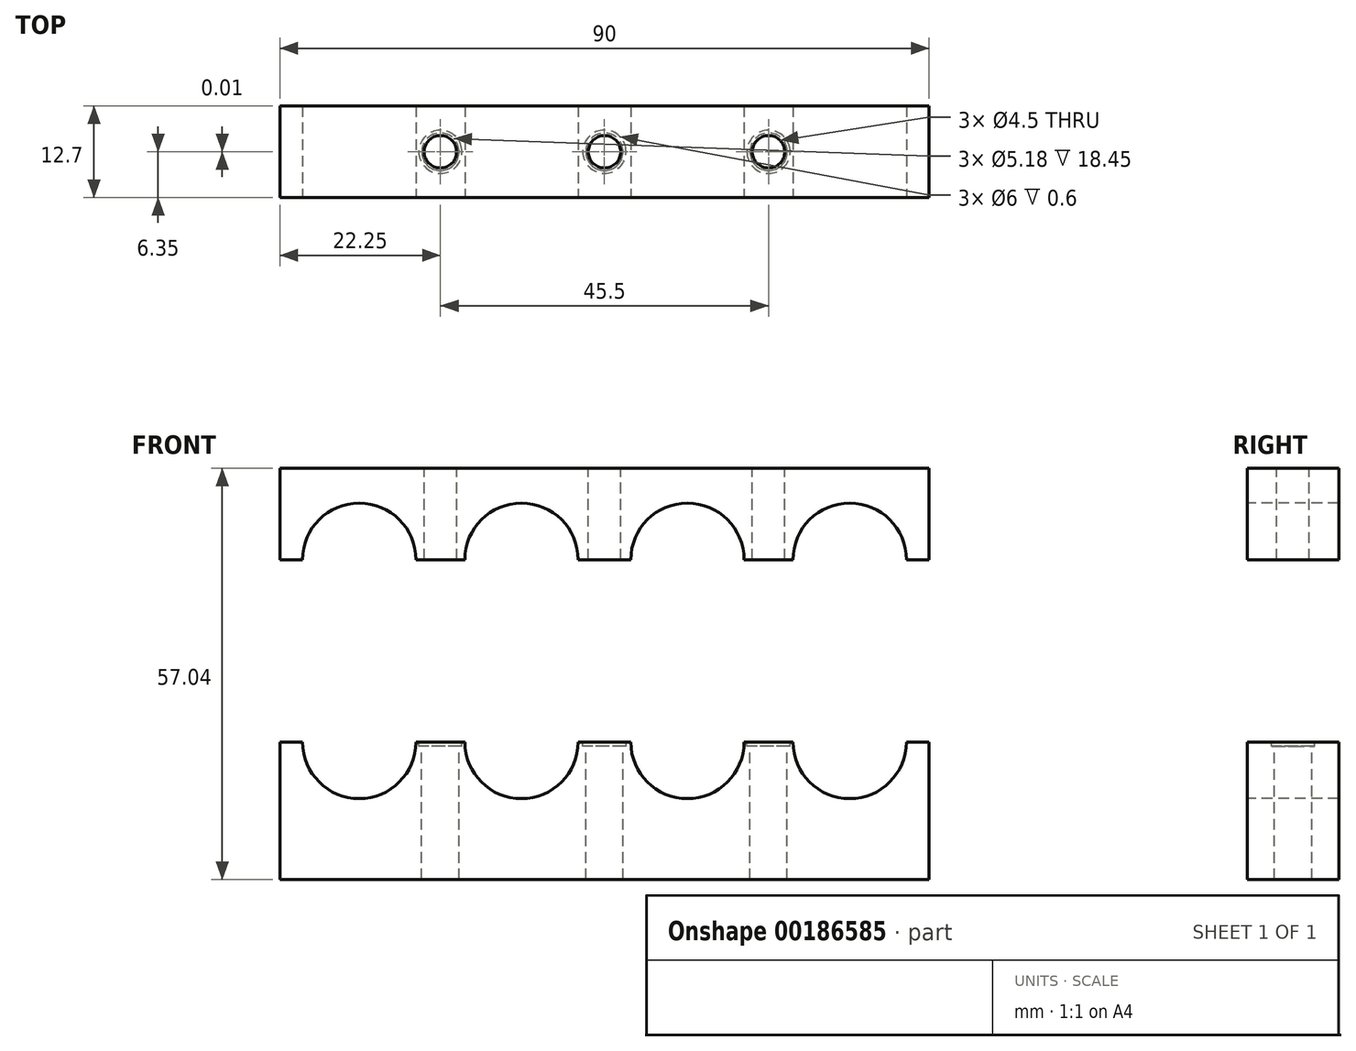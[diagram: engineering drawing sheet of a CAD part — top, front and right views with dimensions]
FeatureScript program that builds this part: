
annotation { "Feature Type Name" : "Feature", "Feature Type Description" : "" }
export const myFeature = defineFeature(function(context is Context, id is Id, definition is map)
    precondition{}
    {
        {
            var Q0;
            Q0=qCreatedBy(makeId("Front.planeOp"),FACE);
            var sketch = newSketch(context, id + "F0", { "sketchPlane" : qUnion([Q0])});
            skLineSegment(sketch, "E0.bottom", {"start": v(45, 9.52) * mm, "end": v(-45, 9.53) * mm});
            skLineSegment(sketch, "E0.top", {"start": v(45, -9.53) * mm, "end": v(-45, -9.52) * mm});
            skLineSegment(sketch, "E0.left", {"start": v(45, 9.52) * mm, "end": v(45, -9.53) * mm});
            skLineSegment(sketch, "E0.right", {"start": v(-45, 9.53) * mm, "end": v(-45, -9.52) * mm});
            skPoint(sketch, "E0.middle", {"position": v(0, 0) * mm});
            skSolve(sketch);
        }
        {
            var Q0;
            Q0 = qSketchRegion(id + "F0", true);
            extrude(context, id + "F1", {"entities" : qUnion([Q0]), "depth" : 12.7 * mm});
        }
        {
            var Q0;
            Q0=makeQuery(id+"F1.opExtrude","CAP_FACE",FACE,{"disambiguationData":[OSD([sQuery(id+"F0.wireOp",EDGE,"E0.bottom"),sQuery(id+"F0.wireOp",EDGE,"E0.top"),sQuery(id+"F0.wireOp",EDGE,"E0.left"),sQuery(id+"F0.wireOp",EDGE,"E0.right")])],"isStart":false});
            var sketch = newSketch(context, id + "F2", { "sketchPlane" : qUnion([Q0])});
            skCircle(sketch, "E1", {"center": v(-34, 9.52) * mm, "radius": 7.85 * mm});
            skCircle(sketch, "E2", {"center": v(-11.5, 9.52) * mm, "radius": 7.85 * mm});
            skCircle(sketch, "E3.MirrorC", {"center": v(11.5, 9.52) * mm, "radius": 7.85 * mm});
            skCircle(sketch, "E4.MirrorC", {"center": v(34, 9.52) * mm, "radius": 7.85 * mm});
            skSolve(sketch);
        }
        {
            var Q0;
            Q0 = qSketchRegion(id + "F2", true);
            extrude(context, id + "F3", {"entities" : qUnion([Q0]), "operationType" : NewBodyOperationType.REMOVE, "oppositeDirection" : true, "depth" : 25.4 * mm});
        }
        {
            var Q0;
            Q0=qCreatedBy(makeId("Front.planeOp"),FACE);
            var sketch = newSketch(context, id + "F4", { "sketchPlane" : qUnion([Q0])});
            skLineSegment(sketch, "E5.bottom", {"start": v(45, 34.81) * mm, "end": v(-45, 34.81) * mm});
            skLineSegment(sketch, "E5.top", {"start": v(45, 47.51) * mm, "end": v(-45, 47.51) * mm});
            skLineSegment(sketch, "E5.left", {"start": v(45, 34.81) * mm, "end": v(45, 47.51) * mm});
            skLineSegment(sketch, "E5.right", {"start": v(-45, 34.81) * mm, "end": v(-45, 47.51) * mm});
            skPoint(sketch, "E5.middle", {"position": v(0, 41.16) * mm});
            skSolve(sketch);
        }
        {
            var Q0;
            Q0=makeQuery(id+"F4.imprint","IMPRINT",FACE,{"disambiguationData":[TD([[makeQuery(id+"F4.imprint","IMPRINT",EDGE,{"derivedFrom":sQuery(id+"F4.wireOp",EDGE,"E5.bottom")}),-1.0]])]});
            extrude(context, id + "F5", {"entities" : qUnion([Q0]), "depth" : 12.7 * mm});
        }
        {
            var Q0;
            Q0=makeQuery(id+"F5.opExtrude","CAP_FACE",FACE,{"disambiguationData":[OSD([sQuery(id+"F4.wireOp",EDGE,"E5.bottom"),sQuery(id+"F4.wireOp",EDGE,"E5.top"),sQuery(id+"F4.wireOp",EDGE,"E5.left"),sQuery(id+"F4.wireOp",EDGE,"E5.right")])],"isStart":false});
            var sketch = newSketch(context, id + "F6", { "sketchPlane" : qUnion([Q0])});
            skCircle(sketch, "E6", {"center": v(-34, 34.81) * mm, "radius": 7.85 * mm});
            skCircle(sketch, "E7", {"center": v(-11.5, 34.81) * mm, "radius": 7.85 * mm});
            skCircle(sketch, "E8.MirrorC", {"center": v(11.5, 34.81) * mm, "radius": 7.85 * mm});
            skCircle(sketch, "E9.MirrorC", {"center": v(34, 34.81) * mm, "radius": 7.85 * mm});
            skSolve(sketch);
        }
        {
            var Q0;
            Q0 = qSketchRegion(id + "F6", true);
            extrude(context, id + "F7", {"entities" : qUnion([Q0]), "operationType" : NewBodyOperationType.REMOVE, "oppositeDirection" : true, "depth" : 25.4 * mm});
        }
        {
            var Q0;
            Q0=makeQuery(id+"F5.opExtrude","SWEPT_FACE",FACE,{"disambiguationData":[OSD([sQuery(id+"F4.wireOp",EDGE,"E5.top")])]});
            var sketch = newSketch(context, id + "F8", { "sketchPlane" : qUnion([Q0])});
            skCircle(sketch, "E10", {"center": v(-22.75, -6.35) * mm, "radius": 2.25 * mm});
            skCircle(sketch, "E11", {"center": v(0, -6.35) * mm, "radius": 2.25 * mm});
            skCircle(sketch, "E12", {"center": v(22.75, -6.35) * mm, "radius": 2.25 * mm});
            skSolve(sketch);
        }
        {
            var Q0;
            Q0 = qSketchRegion(id + "F8", true);
            extrude(context, id + "F9", {"entities" : qUnion([Q0]), "operationType" : NewBodyOperationType.REMOVE, "oppositeDirection" : true, "depth" : 25.4 * mm});
        }
        {
            var Q0;
            {var subQ0=sQuery(id+"F0.wireOp",EDGE,"E0.right");var subQ1=sQuery(id+"F0.wireOp",EDGE,"E0.left");var subQ2=sQuery(id+"F0.wireOp",EDGE,"E0.top");var subQ3=sQuery(id+"F0.wireOp",EDGE,"E0.bottom");Q0=makeQuery(id+"F3.boolean.opBoolean","SPLIT",FACE,{"disambiguationData":[TD([makeQuery(id+"F1.opExtrude","CAP_FACE",FACE,{"disambiguationData":[OSD([subQ3,subQ2,subQ1,subQ0])],"isStart":true}),makeQuery(id+"F1.opExtrude","CAP_FACE",FACE,{"disambiguationData":[OSD([subQ3,subQ2,subQ1,subQ0])],"isStart":false}),makeQuery(id+"F3.opExtrude","SWEPT_FACE",FACE,{"disambiguationData":[OSD([sQuery(id+"F2.wireOp",EDGE,"E1")])]}),makeQuery(id+"F3.opExtrude","SWEPT_FACE",FACE,{"disambiguationData":[OSD([sQuery(id+"F2.wireOp",EDGE,"E2")])]})])],"derivedFrom":makeQuery(id+"F1.opExtrude","SWEPT_FACE",FACE,{"disambiguationData":[OSD([subQ3])]})});}
            var sketch = newSketch(context, id + "F10", { "sketchPlane" : qUnion([Q0])});
            skCircle(sketch, "E13", {"center": v(-22.75, -6.35) * mm, "radius": 2.6 * mm});
            skCircle(sketch, "E14", {"center": v(0, -6.35) * mm, "radius": 2.6 * mm});
            skCircle(sketch, "E15", {"center": v(22.75, -6.35) * mm, "radius": 2.6 * mm});
            skSolve(sketch);
        }
        {
            var Q0;
            Q0 = qSketchRegion(id + "F10", true);
            extrude(context, id + "F11", {"entities" : qUnion([Q0]), "operationType" : NewBodyOperationType.REMOVE, "oppositeDirection" : true, "depth" : 20 * mm});
        }
        {
            var Q0;
            {var subQ0=sQuery(id+"F0.wireOp",EDGE,"E0.right");var subQ1=sQuery(id+"F0.wireOp",EDGE,"E0.left");var subQ2=sQuery(id+"F0.wireOp",EDGE,"E0.top");var subQ3=sQuery(id+"F0.wireOp",EDGE,"E0.bottom");Q0=makeQuery(id+"F3.boolean.opBoolean","SPLIT",FACE,{"disambiguationData":[TD([makeQuery(id+"F1.opExtrude","CAP_FACE",FACE,{"disambiguationData":[OSD([subQ3,subQ2,subQ1,subQ0])],"isStart":true}),makeQuery(id+"F1.opExtrude","CAP_FACE",FACE,{"disambiguationData":[OSD([subQ3,subQ2,subQ1,subQ0])],"isStart":false}),makeQuery(id+"F3.opExtrude","SWEPT_FACE",FACE,{"disambiguationData":[OSD([sQuery(id+"F2.wireOp",EDGE,"E1")])]}),makeQuery(id+"F3.opExtrude","SWEPT_FACE",FACE,{"disambiguationData":[OSD([sQuery(id+"F2.wireOp",EDGE,"E2")])]})])],"derivedFrom":makeQuery(id+"F1.opExtrude","SWEPT_FACE",FACE,{"disambiguationData":[OSD([subQ3])]})});}
            var sketch = newSketch(context, id + "F12", { "sketchPlane" : qUnion([Q0])});
            skCircle(sketch, "E16", {"center": v(-22.75, -6.35) * mm, "radius": 3 * mm});
            skCircle(sketch, "E17.MirrorC", {"center": v(22.75, -6.35) * mm, "radius": 3 * mm});
            skCircle(sketch, "E18", {"center": v(0, -6.34) * mm, "radius": 3 * mm});
            skSolve(sketch);
        }
        {
            var Q0;
            Q0 = qSketchRegion(id + "F12", true);
            extrude(context, id + "F13", {"entities" : qUnion([Q0]), "operationType" : NewBodyOperationType.REMOVE, "oppositeDirection" : true, "depth" : 0.5 * mm});
        }
        {
            var Q0;
            Q0 = qSketchRegion(id + "F12", true);
            extrude(context, id + "F14", {"entities" : qUnion([Q0]), "operationType" : NewBodyOperationType.REMOVE, "oppositeDirection" : true, "depth" : 0.6 * mm});
        }
    });
